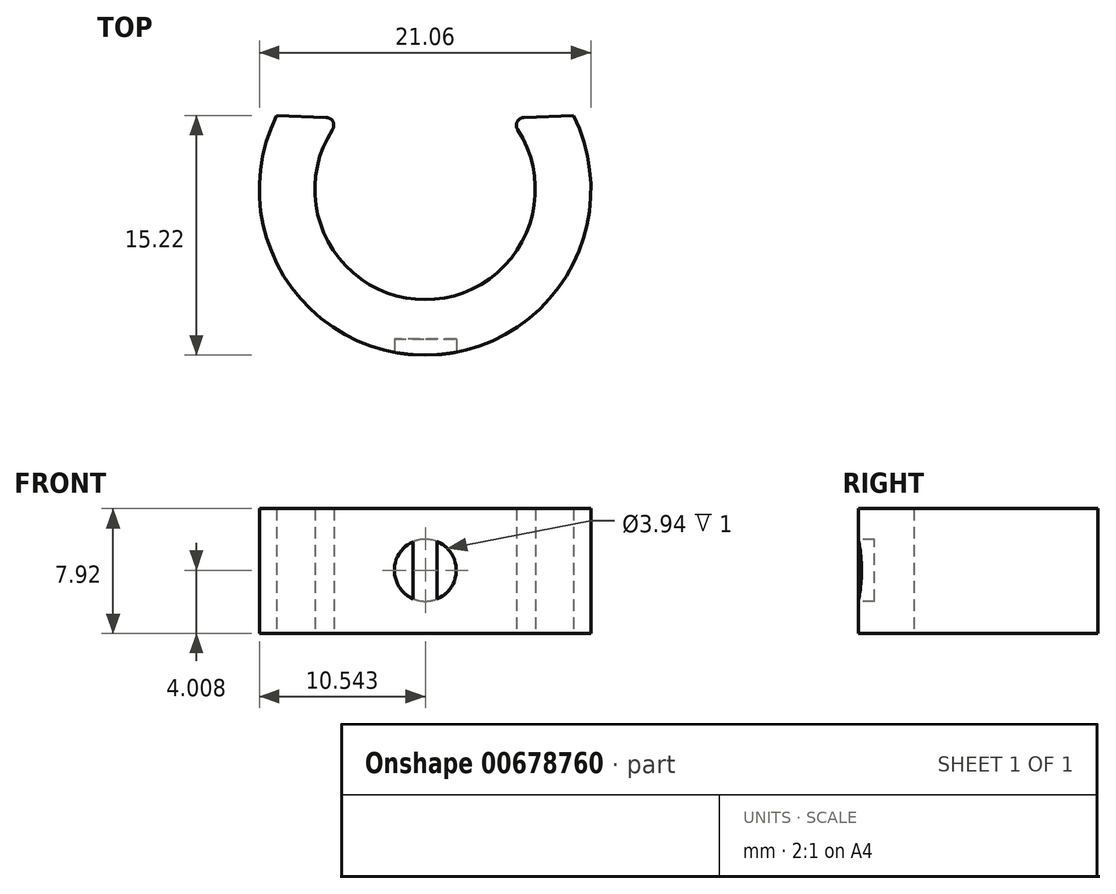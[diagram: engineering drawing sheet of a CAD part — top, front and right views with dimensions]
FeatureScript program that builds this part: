
annotation { "Feature Type Name" : "Feature", "Feature Type Description" : "" }
export const myFeature = defineFeature(function(context is Context, id is Id, definition is map)
    precondition{}
    {
        {
            var Q0;
            Q0=qCreatedBy(makeId("Top.planeOp"),FACE);
            var sketch = newSketch(context, id + "F0", { "sketchPlane" : qUnion([Q0])});
            skArc(sketch, "E0", {"start": v(-5.33, 4.54) * mm, "mid": v(0, -7) * mm, "end": v(5.33, 4.54) * mm});
            skLineSegment(sketch, "E1", {"start": v(-5.33, 4.54) * mm, "end": v(5.33, 4.54) * mm, "construction": true});
            skSolve(sketch);
        }
        {
            var Q0;
            Q0=qCreatedBy(makeId("Top.planeOp"),FACE);
            var sketch = newSketch(context, id + "F1", { "sketchPlane" : qUnion([Q0])});
            skLineSegment(sketch, "E2", {"start": v(-6.99, 0) * mm, "end": v(7.03, 0) * mm, "construction": true});
            skArc(sketch, "E3", {"start": v(-9.43, 4.69) * mm, "mid": v(0, -10.53) * mm, "end": v(9.43, 4.69) * mm});
            skLineSegment(sketch, "E4", {"start": v(-9.43, 4.69) * mm, "end": v(9.43, 4.69) * mm, "construction": true});
            skArc(sketch, "E5.1", {"start": v(-5.33, 4.54) * mm, "mid": v(0, -7) * mm, "end": v(5.33, 4.54) * mm});
            skLineSegment(sketch, "E6", {"start": v(-9.43, 4.69) * mm, "end": v(-5.33, 4.54) * mm});
            skLineSegment(sketch, "E7", {"start": v(5.33, 4.54) * mm, "end": v(9.43, 4.69) * mm});
            skSolve(sketch);
        }
        {
            var Q0;
            Q0 = qSketchRegion(id + "F1", true);
            extrude(context, id + "F2", {"entities" : qUnion([Q0]), "depth" : 7.92 * mm, "offsetDistance" : 25 * mm});
        }
        {
            var Q0;
            Q0=makeQuery(id+"F2.opExtrude","SWEPT_EDGE",EDGE,{"disambiguationData":[OSD([sQuery(id+"F1.wireOp",EDGE,"E5.1"),sQuery(id+"F1.wireOp",EDGE,"E6")])]});
            var Q1;
            Q1=makeQuery(id+"F2.opExtrude","SWEPT_EDGE",EDGE,{"disambiguationData":[OSD([sQuery(id+"F1.wireOp",EDGE,"E5.1"),sQuery(id+"F1.wireOp",EDGE,"E7")])]});
            fillet(context, id + "F3", {"entities" : qUnion([Q0, Q1]), "radius" : .5 * mm, "tangentPropagation" : true, "allowEdgeOverflow" : false});
        }
        {
            var Q0;
            Q0=qCreatedBy(makeId("Front.planeOp"),FACE);
            cPlane(context, id + "F4", {"entities" : qUnion([Q0]), "cplaneType" : CPlaneType.OFFSET, "offset" : 10.5 * mm, "width" : 150 * mm, "height" : 150 * mm});
        }
        {
            var Q0;
            Q0=qCreatedBy(id+"F4.planeOp",FACE);
            var sketch = newSketch(context, id + "F5", { "sketchPlane" : qUnion([Q0])});
            skCircle(sketch, "E8", {"center": v(0.01, 4) * mm, "radius": 1.97 * mm});
            skPoint(sketch, "E8.first.point", {"position": v(0, 2.04) * mm});
            skPoint(sketch, "E8.second.point", {"position": v(0, 5.98) * mm});
            skPoint(sketch, "E8.third.point", {"position": v(-1.79, 3.21) * mm});
            skSolve(sketch);
        }
        {
            var Q0;
            Q0 = qSketchRegion(id + "F5", true);
            extrude(context, id + "F6", {"entities" : qUnion([Q0]), "operationType" : NewBodyOperationType.REMOVE, "oppositeDirection" : true, "depth" : 1 * mm, "offsetDistance" : 25 * mm});
        }
    });
